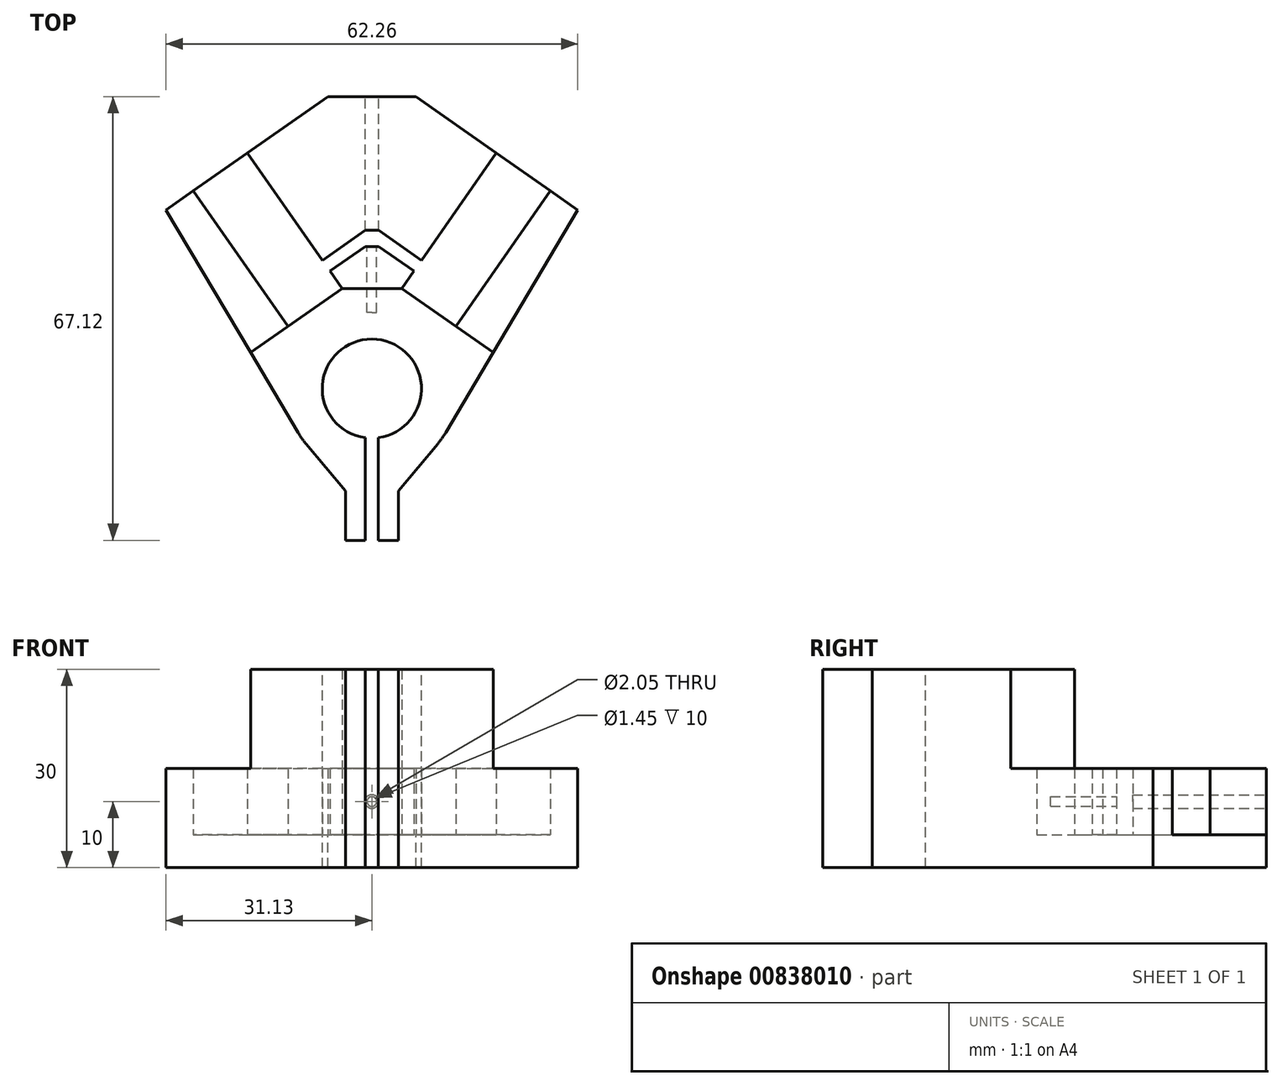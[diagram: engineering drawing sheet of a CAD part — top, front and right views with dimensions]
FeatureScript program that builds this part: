
annotation { "Feature Type Name" : "Feature", "Feature Type Description" : "" }
export const myFeature = defineFeature(function(context is Context, id is Id, definition is map)
    precondition{}
    {
        {
            assignVariable(context, id + "F0", {"name" : "InsertWidth", "anyValue" : 10});
        }
        {
            var Q0;
            Q0=qCreatedBy(makeId("Top.planeOp"),FACE);
            var sketch = newSketch(context, id + "F1", { "sketchPlane" : qUnion([Q0])});
            skPoint(sketch, "E0", {"position": v(-20.9, -11.5) * mm});
            skArc(sketch, "E1", {"start": v(-20.9, -4) * mm, "mid": v(-28.4, -11.5) * mm, "end": v(-20.9, -19) * mm});
            skArc(sketch, "E2", {"start": v(-20.9, 1.5) * mm, "mid": v(-33.9, -11.5) * mm, "end": v(-20.9, -24.5) * mm});
            skLineSegment(sketch, "E3", {"start": v(-20.9, -11.5) * mm, "end": v(-75.55, 66.56) * mm, "construction": true});
            skLineSegment(sketch, "E4", {"start": v(-20.9, -11.5) * mm, "end": v(-20.9, 94.88) * mm, "construction": true});
            skLineSegment(sketch, "E5", {"start": v(-21.62, 32.66) * mm, "end": v(-21.62, 36.51) * mm, "construction": true});
            skLineSegment(sketch, "E6", {"start": v(-33.6, -2.08) * mm, "end": v(-25.4, 3.66) * mm});
            skPoint(sketch, "E7", {"position": v(-29.5, 0.8) * mm});
            skLineSegment(sketch, "E8", {"start": v(-25.4, 3.66) * mm, "end": v(-39.75, 24.14) * mm});
            skPoint(sketch, "E9", {"position": v(-21.62, 0) * mm});
            skLineSegment(sketch, "E10", {"start": v(-21.62, 0) * mm, "end": v(-20.9, 0) * mm});
            skLineSegment(sketch, "E11", {"start": v(-21.62, 0) * mm, "end": v(-21.62, 10) * mm});
            skLineSegment(sketch, "E12", {"start": v(-21.62, 10) * mm, "end": v(-21.92, 10) * mm});
            skLineSegment(sketch, "E13", {"start": v(-21.92, 10) * mm, "end": v(-21.92, 32.66) * mm});
            skLineSegment(sketch, "E14", {"start": v(-33.6, -2.08) * mm, "end": v(-47.94, 18.4) * mm});
            skLineSegment(sketch, "E15", {"start": v(-47.94, 18.4) * mm, "end": v(-39.75, 24.14) * mm});
            skLineSegment(sketch, "E16", {"start": v(-47.94, 18.4) * mm, "end": v(-52.03, 15.53) * mm});
            skLineSegment(sketch, "E17", {"start": v(-39.75, 24.14) * mm, "end": v(-38.93, 24.71) * mm});
            skLineSegment(sketch, "E18", {"start": v(-38.93, 24.71) * mm, "end": v(-21.62, 0) * mm, "construction": true});
            skLineSegment(sketch, "E19", {"start": v(-21.92, 10) * mm, "end": v(-27.24, 6.28) * mm});
            skLineSegment(sketch, "E20", {"start": v(-28.39, 7.92) * mm, "end": v(-21.92, 12.44) * mm});
            skLineSegment(sketch, "E21", {"start": v(-27.57, 8.49) * mm, "end": v(-27.57, 32.66) * mm});
            skLineSegment(sketch, "E22", {"start": v(-38.93, 24.71) * mm, "end": v(-27.57, 32.66) * mm});
            skLineSegment(sketch, "E23", {"start": v(-27.57, 32.66) * mm, "end": v(-20.9, 32.66) * mm});
            skLineSegment(sketch, "E24", {"start": v(-52.03, 15.53) * mm, "end": v(-32.08, -18.12) * mm});
            skPoint(sketch, "E25", {"position": v(-21.9, -24.46) * mm});
            skPoint(sketch, "E26", {"position": v(-21.9, -18.93) * mm});
            skLineSegment(sketch, "E27", {"start": v(-21.9, -18.93) * mm, "end": v(-21.9, -24.46) * mm});
            skLineSegment(sketch, "E28", {"start": v(-21.9, -24.46) * mm, "end": v(-21.9, -34.46) * mm});
            skLineSegment(sketch, "E29", {"start": v(-21.9, -34.46) * mm, "end": v(-24.9, -34.46) * mm});
            skLineSegment(sketch, "E30", {"start": v(-24.9, -34.46) * mm, "end": v(-24.9, -23.87) * mm});
            skPoint(sketch, "E31", {"position": v(-21.9, -29.46) * mm});
            skLineSegment(sketch, "E32", {"start": v(-21.9, -29.46) * mm, "end": v(-24.9, -29.46) * mm, "construction": true});
            skLineSegment(sketch, "E33", {"start": v(-24.9, -29.46) * mm, "end": v(-24.9, -26.96) * mm, "construction": true});
            skLineSegment(sketch, "E34", {"start": v(-24.9, -26.96) * mm, "end": v(-30.86, -19.85) * mm});
            skLineSegment(sketch, "E35.MirrorCS", {"start": v(-20.17, 10) * mm, "end": v(-19.87, 10) * mm});
            skLineSegment(sketch, "E36.MirrorCS", {"start": v(-20.17, 0) * mm, "end": v(-20.9, 0) * mm});
            skLineSegment(sketch, "E37.MirrorCS", {"start": v(-2.05, 24.14) * mm, "end": v(-2.87, 24.71) * mm});
            skLineSegment(sketch, "E38.MirrorCS", {"start": v(-2.87, 24.71) * mm, "end": v(-14.23, 32.66) * mm});
            skLineSegment(sketch, "E39.MirrorCS", {"start": v(-19.9, -18.93) * mm, "end": v(-19.9, -24.46) * mm});
            skLineSegment(sketch, "E40.MirrorCS", {"start": v(6.14, 18.4) * mm, "end": v(10.23, 15.53) * mm});
            skLineSegment(sketch, "E41.MirrorCS", {"start": v(-16.9, -29.46) * mm, "end": v(-16.9, -26.96) * mm, "construction": true});
            skLineSegment(sketch, "E42.MirrorCS", {"start": v(-20.17, 32.66) * mm, "end": v(-20.17, 36.51) * mm, "construction": true});
            skLineSegment(sketch, "E43.MirrorCS", {"start": v(-19.9, -29.46) * mm, "end": v(-16.9, -29.46) * mm, "construction": true});
            skLineSegment(sketch, "E44.MirrorCS", {"start": v(-19.9, -34.46) * mm, "end": v(-16.9, -34.46) * mm});
            skLineSegment(sketch, "E45.MirrorCS", {"start": v(-8.2, -2.08) * mm, "end": v(-16.4, 3.66) * mm});
            skLineSegment(sketch, "E46.MirrorCS", {"start": v(-19.9, -24.46) * mm, "end": v(-19.9, -34.46) * mm});
            skLineSegment(sketch, "E47.MirrorCS", {"start": v(-14.23, 32.66) * mm, "end": v(-20.9, 32.66) * mm});
            skLineSegment(sketch, "E48.MirrorCS", {"start": v(-19.87, 10) * mm, "end": v(-14.56, 6.28) * mm});
            skLineSegment(sketch, "E49.MirrorCS", {"start": v(-19.87, 10) * mm, "end": v(-19.87, 32.66) * mm});
            skLineSegment(sketch, "E50.MirrorCS", {"start": v(-13.41, 7.92) * mm, "end": v(-19.87, 12.44) * mm});
            skLineSegment(sketch, "E51.MirrorCS", {"start": v(-16.9, -26.96) * mm, "end": v(-10.94, -19.85) * mm});
            skLineSegment(sketch, "E52.MirrorCS", {"start": v(10.23, 15.53) * mm, "end": v(-9.72, -18.12) * mm});
            skLineSegment(sketch, "E53.MirrorCS", {"start": v(-8.2, -2.08) * mm, "end": v(6.14, 18.4) * mm});
            skPoint(sketch, "E54.MirrorP", {"position": v(-19.9, -29.46) * mm});
            skLineSegment(sketch, "E55.MirrorCS", {"start": v(-2.87, 24.71) * mm, "end": v(-20.17, 0) * mm, "construction": true});
            skArc(sketch, "E56.MirrorCS", {"start": v(-20.9, 1.5) * mm, "mid": v(-7.9, -11.5) * mm, "end": v(-20.9, -24.5) * mm});
            skPoint(sketch, "E57.MirrorP", {"position": v(-12.3, 0.8) * mm});
            skLineSegment(sketch, "E58.MirrorCS", {"start": v(6.14, 18.4) * mm, "end": v(-2.05, 24.14) * mm});
            skPoint(sketch, "E59.MirrorP", {"position": v(-19.9, -24.46) * mm});
            skLineSegment(sketch, "E60.MirrorCS", {"start": v(-16.9, -34.46) * mm, "end": v(-16.9, -23.87) * mm});
            skLineSegment(sketch, "E61.MirrorCS", {"start": v(-20.17, 0) * mm, "end": v(-20.17, 10) * mm});
            skLineSegment(sketch, "E62.MirrorCS", {"start": v(-16.4, 3.66) * mm, "end": v(-2.05, 24.14) * mm});
            skArc(sketch, "E63.MirrorCS", {"start": v(-20.9, -4) * mm, "mid": v(-13.4, -11.5) * mm, "end": v(-20.9, -19) * mm});
            skLineSegment(sketch, "E64.MirrorCS", {"start": v(-14.23, 8.49) * mm, "end": v(-14.23, 32.66) * mm});
            skPoint(sketch, "E65.MirrorP", {"position": v(-20.17, 0) * mm});
            skPoint(sketch, "E66.MirrorP", {"position": v(-19.9, -18.93) * mm});
            skLineSegment(sketch, "E67", {"start": v(-21.92, 12.44) * mm, "end": v(-19.87, 12.44) * mm});
            skLineSegment(sketch, "E68", {"start": v(-20.17, 10) * mm, "end": v(-21.62, 10) * mm});
            skLineSegment(sketch, "E69", {"start": v(-33.6, -2.08) * mm, "end": v(-39.25, -6.03) * mm});
            skLineSegment(sketch, "E70", {"start": v(-8.2, -2.08) * mm, "end": v(-2.55, -6.03) * mm});
            skLineSegment(sketch, "E71", {"start": v(-25.4, 3.66) * mm, "end": v(-16.4, 3.66) * mm});
            skLineSegment(sketch, "E72", {"start": v(-20.9, -11.5) * mm, "end": v(-37.28, -22.97) * mm, "construction": true});
            skSolve(sketch);
        }
        {
            var Q0;
            {var subQ2=sQuery(id+"F1.wireOp",EDGE,"E21");Q0=makeQuery(id+"F1.imprint","IMPRINT",FACE,{"disambiguationData":[TD([[makeQuery(id+"F1.imprint","IMPRINT",EDGE,{"derivedFrom":subQ2}),1.0]])]});}
            var Q1;
            {var subQ1=sQuery(id+"F1.wireOp",EDGE,"E45.MirrorCS");Q1=makeQuery(id+"F1.imprint","IMPRINT",FACE,{"disambiguationData":[TD([[makeQuery(id+"F1.imprint","IMPRINT",EDGE,{"derivedFrom":subQ1}),-1.0]])]});}
            var Q2;
            {var subQ5=sQuery(id+"F1.wireOp",EDGE,"E27");Q2=makeQuery(id+"F1.imprint","IMPRINT",FACE,{"disambiguationData":[TD([[makeQuery(id+"F1.imprint","IMPRINT",EDGE,{"derivedFrom":subQ5}),-1.0]])]});}
            var Q3;
            {var subQ1=sQuery(id+"F1.wireOp",EDGE,"E12");Q3=makeQuery(id+"F1.imprint","IMPRINT",FACE,{"disambiguationData":[TD([[makeQuery(id+"F1.imprint","IMPRINT",EDGE,{"derivedFrom":subQ1}),1.0]])]});}
            var Q4;
            {var subQ4=sQuery(id+"F1.wireOp",EDGE,"E44.MirrorCS");Q4=makeQuery(id+"F1.imprint","IMPRINT",FACE,{"disambiguationData":[TD([[makeQuery(id+"F1.imprint","IMPRINT",EDGE,{"derivedFrom":subQ4}),1.0]])]});}
            var Q5;
            Q5=makeQuery(id+"F1.imprint","IMPRINT",FACE,{"disambiguationData":[TD([[makeQuery(id+"F1.imprint","IMPRINT",EDGE,{"derivedFrom":sQuery(id+"F1.wireOp",EDGE,"E14")}),1.0]])]});
            var Q6;
            {var subQ0=sQuery(id+"F1.wireOp",EDGE,"E40.MirrorCS");Q6=makeQuery(id+"F1.imprint","IMPRINT",FACE,{"disambiguationData":[TD([[makeQuery(id+"F1.imprint","IMPRINT",EDGE,{"derivedFrom":subQ0}),-1.0]])]});}
            var Q7;
            {var subQ3=sQuery(id+"F1.wireOp",EDGE,"E19");var subQ5=sQuery(id+"F1.wireOp",EDGE,"E18");var subQ6=makeQuery(id+"F1.imprint","INTERSECT",VERTEX,{"derivedFrom":[subQ5,subQ3]});Q7=makeQuery(id+"F1.imprint","IMPRINT",FACE,{"disambiguationData":[TD([[makeQuery(id+"F1.imprint","IMPRINT",EDGE,{"disambiguationData":[TD([[subQ6,-1.0]])],"derivedFrom":subQ5}),-1.0]])]});}
            var Q8;
            {var subQ1=sQuery(id+"F1.wireOp",EDGE,"E35.MirrorCS");Q8=makeQuery(id+"F1.imprint","IMPRINT",FACE,{"disambiguationData":[TD([[makeQuery(id+"F1.imprint","IMPRINT",EDGE,{"derivedFrom":subQ1}),-1.0]])]});}
            var Q9;
            {var subQ0=sQuery(id+"F1.wireOp",EDGE,"E19");var subQ5=sQuery(id+"F1.wireOp",EDGE,"E18");var subQ6=makeQuery(id+"F1.imprint","INTERSECT",VERTEX,{"derivedFrom":[subQ5,subQ0]});Q9=makeQuery(id+"F1.imprint","IMPRINT",FACE,{"disambiguationData":[TD([[makeQuery(id+"F1.imprint","IMPRINT",EDGE,{"disambiguationData":[TD([[subQ6,1.0]])],"derivedFrom":subQ5}),1.0]])]});}
            var Q10;
            {var subQ3=sQuery(id+"F1.wireOp",EDGE,"E28");Q10=makeQuery(id+"F1.imprint","IMPRINT",FACE,{"disambiguationData":[TD([[makeQuery(id+"F1.imprint","IMPRINT",EDGE,{"derivedFrom":subQ3}),-1.0]])]});}
            var Q11;
            {var subQ0=sQuery(id+"F1.wireOp",EDGE,"E51.MirrorCS");Q11=makeQuery(id+"F1.imprint","IMPRINT",FACE,{"disambiguationData":[TD([[makeQuery(id+"F1.imprint","IMPRINT",EDGE,{"derivedFrom":subQ0}),1.0]])]});}
            var Q12;
            {var subQ4=sQuery(id+"F1.wireOp",EDGE,"E6");Q12=makeQuery(id+"F1.imprint","IMPRINT",FACE,{"disambiguationData":[TD([[makeQuery(id+"F1.imprint","IMPRINT",EDGE,{"derivedFrom":subQ4}),1.0]])]});}
            var Q13;
            {var subQ0=sQuery(id+"F1.wireOp",EDGE,"E38.MirrorCS");Q13=makeQuery(id+"F1.imprint","IMPRINT",FACE,{"disambiguationData":[TD([[makeQuery(id+"F1.imprint","IMPRINT",EDGE,{"derivedFrom":subQ0}),1.0]])]});}
            var Q14;
            {var subQ0=sQuery(id+"F1.wireOp",EDGE,"E37.MirrorCS");Q14=makeQuery(id+"F1.imprint","IMPRINT",FACE,{"disambiguationData":[TD([[makeQuery(id+"F1.imprint","IMPRINT",EDGE,{"derivedFrom":subQ0}),1.0]])]});}
            var Q15;
            {var subQ0=sQuery(id+"F1.wireOp",EDGE,"E68");Q15=makeQuery(id+"F1.imprint","IMPRINT",FACE,{"disambiguationData":[TD([[makeQuery(id+"F1.imprint","IMPRINT",EDGE,{"derivedFrom":subQ0}),1.0]])]});}
            var Q16;
            {var subQ3=sQuery(id+"F1.wireOp",EDGE,"E34");Q16=makeQuery(id+"F1.imprint","IMPRINT",FACE,{"disambiguationData":[TD([[makeQuery(id+"F1.imprint","IMPRINT",EDGE,{"derivedFrom":subQ3}),-1.0]])]});}
            var Q17;
            {var subQ5=sQuery(id+"F1.wireOp",EDGE,"E21");Q17=makeQuery(id+"F1.imprint","IMPRINT",FACE,{"disambiguationData":[TD([[makeQuery(id+"F1.imprint","IMPRINT",EDGE,{"derivedFrom":subQ5}),-1.0]])]});}
            var Q18;
            {var subQ3=sQuery(id+"F1.wireOp",EDGE,"E67");Q18=makeQuery(id+"F1.imprint","IMPRINT",FACE,{"disambiguationData":[TD([[makeQuery(id+"F1.imprint","IMPRINT",EDGE,{"derivedFrom":subQ3}),1.0]])]});}
            var Q19;
            {var subQ15=sQuery(id+"F1.wireOp",EDGE,"E6");Q19=makeQuery(id+"F1.imprint","IMPRINT",FACE,{"disambiguationData":[TD([[makeQuery(id+"F1.imprint","IMPRINT",EDGE,{"derivedFrom":subQ15}),-1.0]])]});}
            var Q20;
            {var subQ0=sQuery(id+"F1.wireOp",EDGE,"E64.MirrorCS");Q20=makeQuery(id+"F1.imprint","IMPRINT",FACE,{"disambiguationData":[TD([[makeQuery(id+"F1.imprint","IMPRINT",EDGE,{"derivedFrom":subQ0}),1.0]])]});}
            var Q21;
            {var subQ0=sQuery(id+"F1.wireOp",EDGE,"E17");Q21=makeQuery(id+"F1.imprint","IMPRINT",FACE,{"disambiguationData":[TD([[makeQuery(id+"F1.imprint","IMPRINT",EDGE,{"derivedFrom":subQ0}),-1.0]])]});}
            var Q22;
            {var subQ1=sQuery(id+"F1.wireOp",EDGE,"E48.MirrorCS");var subQ3=sQuery(id+"F1.wireOp",EDGE,"E55.MirrorCS");var subQ4=makeQuery(id+"F1.imprint","INTERSECT",VERTEX,{"derivedFrom":[subQ1,subQ3]});Q22=makeQuery(id+"F1.imprint","IMPRINT",FACE,{"disambiguationData":[TD([[makeQuery(id+"F1.imprint","IMPRINT",EDGE,{"disambiguationData":[TD([[subQ4,1.0]])],"derivedFrom":subQ1}),1.0]])]});}
            var Q23;
            {var subQ0=sQuery(id+"F1.wireOp",EDGE,"E62.MirrorCS");var subQ1=sQuery(id+"F1.wireOp",EDGE,"E48.MirrorCS");var subQ2=makeQuery(id+"F1.imprint","INTERSECT",VERTEX,{"derivedFrom":[subQ1,subQ0]});Q23=makeQuery(id+"F1.imprint","IMPRINT",FACE,{"disambiguationData":[TD([[makeQuery(id+"F1.imprint","IMPRINT",EDGE,{"disambiguationData":[TD([[subQ2,1.0]])],"derivedFrom":subQ1}),-1.0]])]});}
            var Q24;
            {var subQ1=sQuery(id+"F1.wireOp",EDGE,"E11");var subQ3=sQuery(id+"F1.wireOp",EDGE,"E71");var subQ4=makeQuery(id+"F1.imprint","INTERSECT",VERTEX,{"derivedFrom":[subQ1,subQ3]});Q24=makeQuery(id+"F1.imprint","IMPRINT",FACE,{"disambiguationData":[TD([[makeQuery(id+"F1.imprint","IMPRINT",EDGE,{"disambiguationData":[TD([[subQ4,1.0]])],"derivedFrom":subQ3}),-1.0]])]});}
            var Q25;
            {var subQ1=sQuery(id+"F1.wireOp",EDGE,"E55.MirrorCS");var subQ3=sQuery(id+"F1.wireOp",EDGE,"E71");var subQ4=makeQuery(id+"F1.imprint","INTERSECT",VERTEX,{"derivedFrom":[subQ1,subQ3]});Q25=makeQuery(id+"F1.imprint","IMPRINT",FACE,{"disambiguationData":[TD([[makeQuery(id+"F1.imprint","IMPRINT",EDGE,{"disambiguationData":[TD([[subQ4,1.0]])],"derivedFrom":subQ3}),-1.0]])]});}
            var Q26;
            {var subQ5=sQuery(id+"F1.wireOp",EDGE,"E10");Q26=makeQuery(id+"F1.imprint","IMPRINT",FACE,{"disambiguationData":[TD([[makeQuery(id+"F1.imprint","IMPRINT",EDGE,{"derivedFrom":subQ5}),1.0]])]});}
            var Q27;
            {var subQ0=sQuery(id+"F1.wireOp",EDGE,"E62.MirrorCS");var subQ1=sQuery(id+"F1.wireOp",EDGE,"E48.MirrorCS");var subQ2=makeQuery(id+"F1.imprint","INTERSECT",VERTEX,{"derivedFrom":[subQ1,subQ0]});Q27=makeQuery(id+"F1.imprint","IMPRINT",FACE,{"disambiguationData":[TD([[makeQuery(id+"F1.imprint","IMPRINT",EDGE,{"disambiguationData":[TD([[subQ2,1.0]])],"derivedFrom":subQ1}),1.0]])]});}
            var Q28;
            {var subQ0=sQuery(id+"F1.wireOp",EDGE,"E19");var subQ1=sQuery(id+"F1.wireOp",EDGE,"E8");var subQ2=makeQuery(id+"F1.imprint","INTERSECT",VERTEX,{"derivedFrom":[subQ1,subQ0]});Q28=makeQuery(id+"F1.imprint","IMPRINT",FACE,{"disambiguationData":[TD([[makeQuery(id+"F1.imprint","IMPRINT",EDGE,{"disambiguationData":[TD([[subQ2,-1.0]])],"derivedFrom":subQ1}),-1.0]])]});}
            var Q29;
            {var subQ2=sQuery(id+"F1.wireOp",EDGE,"E12");Q29=makeQuery(id+"F1.imprint","IMPRINT",FACE,{"disambiguationData":[TD([[makeQuery(id+"F1.imprint","IMPRINT",EDGE,{"derivedFrom":subQ2}),-1.0]])]});}
            var Q30;
            {var subQ8=sQuery(id+"F1.wireOp",EDGE,"E45.MirrorCS");Q30=makeQuery(id+"F1.imprint","IMPRINT",FACE,{"disambiguationData":[TD([[makeQuery(id+"F1.imprint","IMPRINT",EDGE,{"derivedFrom":subQ8}),1.0]])]});}
            extrude(context, id + "F2", {"entities" : qUnion([Q0, Q1, Q2, Q3, Q4, Q5, Q6, Q7, Q8, Q9, Q10, Q11, Q12, Q13, Q14, Q15, Q16, Q17, Q18, Q19, Q20, Q21, Q22, Q23, Q24, Q25, Q26, Q27, Q28, Q29, Q30]), "oppositeDirection" : true, "depth" : 5 * mm, "offsetDistance" : 25 * mm});
        }
        {
            var Q0;
            {var subQ0=sQuery(id+"F1.wireOp",EDGE,"E64.MirrorCS");Q0=makeQuery(id+"F1.imprint","IMPRINT",FACE,{"disambiguationData":[TD([[makeQuery(id+"F1.imprint","IMPRINT",EDGE,{"derivedFrom":subQ0}),1.0]])]});}
            var Q1;
            {var subQ5=sQuery(id+"F1.wireOp",EDGE,"E21");Q1=makeQuery(id+"F1.imprint","IMPRINT",FACE,{"disambiguationData":[TD([[makeQuery(id+"F1.imprint","IMPRINT",EDGE,{"derivedFrom":subQ5}),-1.0]])]});}
            var Q2;
            {var subQ2=sQuery(id+"F1.wireOp",EDGE,"E21");Q2=makeQuery(id+"F1.imprint","IMPRINT",FACE,{"disambiguationData":[TD([[makeQuery(id+"F1.imprint","IMPRINT",EDGE,{"derivedFrom":subQ2}),1.0]])]});}
            var Q3;
            {var subQ0=sQuery(id+"F1.wireOp",EDGE,"E17");Q3=makeQuery(id+"F1.imprint","IMPRINT",FACE,{"disambiguationData":[TD([[makeQuery(id+"F1.imprint","IMPRINT",EDGE,{"derivedFrom":subQ0}),-1.0]])]});}
            var Q4;
            {var subQ0=sQuery(id+"F1.wireOp",EDGE,"E38.MirrorCS");Q4=makeQuery(id+"F1.imprint","IMPRINT",FACE,{"disambiguationData":[TD([[makeQuery(id+"F1.imprint","IMPRINT",EDGE,{"derivedFrom":subQ0}),1.0]])]});}
            var Q5;
            {var subQ0=sQuery(id+"F1.wireOp",EDGE,"E37.MirrorCS");Q5=makeQuery(id+"F1.imprint","IMPRINT",FACE,{"disambiguationData":[TD([[makeQuery(id+"F1.imprint","IMPRINT",EDGE,{"derivedFrom":subQ0}),1.0]])]});}
            var Q6;
            {var subQ3=sQuery(id+"F1.wireOp",EDGE,"E67");Q6=makeQuery(id+"F1.imprint","IMPRINT",FACE,{"disambiguationData":[TD([[makeQuery(id+"F1.imprint","IMPRINT",EDGE,{"derivedFrom":subQ3}),1.0]])]});}
            extrude(context, id + "F3", {"entities" : qUnion([Q0, Q1, Q2, Q3, Q4, Q5, Q6]), "depth" : (getVariable(context, 'InsertWidth')) * mm, "offsetDistance" : 25 * mm});
        }
        {
            var Q0;
            Q0=makeQuery(id+"F3.opExtrude","SWEPT_FACE",FACE,{"disambiguationData":[OSD([sQuery(id+"F1.wireOp",EDGE,"E23"),sQuery(id+"F1.wireOp",EDGE,"E47.MirrorCS")])]});
            var sketch = newSketch(context, id + "F4", { "sketchPlane" : qUnion([Q0])});
            skPoint(sketch, "E73.0", {"position": v(20.9, 0) * mm});
            skPoint(sketch, "E73.1", {"position": v(21.62, 0) * mm});
            skPoint(sketch, "E73.2", {"position": v(21.92, 0) * mm});
            skPoint(sketch, "E73.3", {"position": v(20.17, 0) * mm});
            skPoint(sketch, "E73.4", {"position": v(19.87, 0) * mm});
            skLineSegment(sketch, "E74", {"start": v(20.9, 0) * mm, "end": v(20.9, 10) * mm, "construction": true});
            skPoint(sketch, "E75", {"position": v(20.9, 5) * mm});
            skLineSegment(sketch, "E76", {"start": v(21.62, 0) * mm, "end": v(21.62, 10) * mm, "construction": true});
            skLineSegment(sketch, "E77", {"start": v(21.92, 0) * mm, "end": v(21.92, 10) * mm, "construction": true});
            skCircle(sketch, "E78", {"center": v(20.9, 5) * mm, "radius": 0.73 * mm});
            skCircle(sketch, "E79", {"center": v(20.9, 5) * mm, "radius": 1.03 * mm});
            skSolve(sketch);
        }
        {
            var Q0;
            {var subQ15=sQuery(id+"F1.wireOp",EDGE,"E6");Q0=makeQuery(id+"F1.imprint","IMPRINT",FACE,{"disambiguationData":[TD([[makeQuery(id+"F1.imprint","IMPRINT",EDGE,{"derivedFrom":subQ15}),-1.0]])]});}
            var Q1;
            {var subQ5=sQuery(id+"F1.wireOp",EDGE,"E27");Q1=makeQuery(id+"F1.imprint","IMPRINT",FACE,{"disambiguationData":[TD([[makeQuery(id+"F1.imprint","IMPRINT",EDGE,{"derivedFrom":subQ5}),-1.0]])]});}
            var Q2;
            {var subQ3=sQuery(id+"F1.wireOp",EDGE,"E28");Q2=makeQuery(id+"F1.imprint","IMPRINT",FACE,{"disambiguationData":[TD([[makeQuery(id+"F1.imprint","IMPRINT",EDGE,{"derivedFrom":subQ3}),-1.0]])]});}
            var Q3;
            {var subQ3=sQuery(id+"F1.wireOp",EDGE,"E34");Q3=makeQuery(id+"F1.imprint","IMPRINT",FACE,{"disambiguationData":[TD([[makeQuery(id+"F1.imprint","IMPRINT",EDGE,{"derivedFrom":subQ3}),-1.0]])]});}
            var Q4;
            {var subQ0=sQuery(id+"F1.wireOp",EDGE,"E51.MirrorCS");Q4=makeQuery(id+"F1.imprint","IMPRINT",FACE,{"disambiguationData":[TD([[makeQuery(id+"F1.imprint","IMPRINT",EDGE,{"derivedFrom":subQ0}),1.0]])]});}
            var Q5;
            {var subQ4=sQuery(id+"F1.wireOp",EDGE,"E44.MirrorCS");Q5=makeQuery(id+"F1.imprint","IMPRINT",FACE,{"disambiguationData":[TD([[makeQuery(id+"F1.imprint","IMPRINT",EDGE,{"derivedFrom":subQ4}),1.0]])]});}
            var Q6;
            {var subQ1=sQuery(id+"F1.wireOp",EDGE,"E55.MirrorCS");var subQ3=sQuery(id+"F1.wireOp",EDGE,"E71");var subQ4=makeQuery(id+"F1.imprint","INTERSECT",VERTEX,{"derivedFrom":[subQ1,subQ3]});Q6=makeQuery(id+"F1.imprint","IMPRINT",FACE,{"disambiguationData":[TD([[makeQuery(id+"F1.imprint","IMPRINT",EDGE,{"disambiguationData":[TD([[subQ4,1.0]])],"derivedFrom":subQ3}),-1.0]])]});}
            var Q7;
            {var subQ1=sQuery(id+"F1.wireOp",EDGE,"E11");var subQ3=sQuery(id+"F1.wireOp",EDGE,"E71");var subQ4=makeQuery(id+"F1.imprint","INTERSECT",VERTEX,{"derivedFrom":[subQ1,subQ3]});Q7=makeQuery(id+"F1.imprint","IMPRINT",FACE,{"disambiguationData":[TD([[makeQuery(id+"F1.imprint","IMPRINT",EDGE,{"disambiguationData":[TD([[subQ4,1.0]])],"derivedFrom":subQ3}),-1.0]])]});}
            var Q8;
            {var subQ5=sQuery(id+"F1.wireOp",EDGE,"E10");Q8=makeQuery(id+"F1.imprint","IMPRINT",FACE,{"disambiguationData":[TD([[makeQuery(id+"F1.imprint","IMPRINT",EDGE,{"derivedFrom":subQ5}),1.0]])]});}
            var Q9;
            {var subQ8=sQuery(id+"F1.wireOp",EDGE,"E45.MirrorCS");Q9=makeQuery(id+"F1.imprint","IMPRINT",FACE,{"disambiguationData":[TD([[makeQuery(id+"F1.imprint","IMPRINT",EDGE,{"derivedFrom":subQ8}),1.0]])]});}
            extrude(context, id + "F5", {"entities" : qUnion([Q0, Q1, Q2, Q3, Q4, Q5, Q6, Q7, Q8, Q9]), "operationType" : NewBodyOperationType.ADD, "depth" : 25 * mm, "offsetDistance" : 25 * mm});
        }
        {
            var Q0;
            {var subQ7=sQuery(id+"F1.wireOp",EDGE,"E27");Q0=makeQuery(id+"F1.imprint","IMPRINT",FACE,{"disambiguationData":[TD([[makeQuery(id+"F1.imprint","IMPRINT",EDGE,{"derivedFrom":subQ7}),-1.0]])]});}
            var Q1;
            {var subQ3=sQuery(id+"F1.wireOp",EDGE,"E34");Q1=makeQuery(id+"F1.imprint","IMPRINT",FACE,{"disambiguationData":[TD([[makeQuery(id+"F1.imprint","IMPRINT",EDGE,{"derivedFrom":subQ3}),-1.0]])]});}
            var Q2;
            {var subQ1=sQuery(id+"F1.wireOp",EDGE,"E28");Q2=makeQuery(id+"F1.imprint","IMPRINT",FACE,{"disambiguationData":[TD([[makeQuery(id+"F1.imprint","IMPRINT",EDGE,{"derivedFrom":subQ1}),-1.0]])]});}
            var Q3;
            {var subQ1=sQuery(id+"F1.wireOp",EDGE,"E44.MirrorCS");Q3=makeQuery(id+"F1.imprint","IMPRINT",FACE,{"disambiguationData":[TD([[makeQuery(id+"F1.imprint","IMPRINT",EDGE,{"derivedFrom":subQ1}),1.0]])]});}
            var Q4;
            {var subQ0=sQuery(id+"F1.wireOp",EDGE,"E51.MirrorCS");Q4=makeQuery(id+"F1.imprint","IMPRINT",FACE,{"disambiguationData":[TD([[makeQuery(id+"F1.imprint","IMPRINT",EDGE,{"derivedFrom":subQ0}),1.0]])]});}
            var Q5;
            {var subQ3=sQuery(id+"F1.wireOp",EDGE,"wE3qk1zT-ZEZv-AR1l-YeVC-WgNcCrWfGm45");Q5=makeQuery(id+"F1.imprint","IMPRINT",FACE,{"disambiguationData":[TD([[makeQuery(id+"F1.imprint","IMPRINT",EDGE,{"derivedFrom":subQ3}),-1.0]])]});}
            var Q6;
            {var subQ3=sQuery(id+"F1.wireOp",EDGE,"uzH9pRL8-awsT-I6LR-pqOu-2XfLFLQ0b1Ti");Q6=makeQuery(id+"F1.imprint","IMPRINT",FACE,{"disambiguationData":[TD([[makeQuery(id+"F1.imprint","IMPRINT",EDGE,{"derivedFrom":subQ3}),1.0]])]});}
            var Q7;
            Q7=makeQuery(id+"F1.imprint","IMPRINT",FACE,{"disambiguationData":[TD([[makeQuery(id+"F1.imprint","IMPRINT",EDGE,{"derivedFrom":sQuery(id+"F1.wireOp",EDGE,"E14")}),1.0]])]});
            var Q8;
            {var subQ0=sQuery(id+"F1.wireOp",EDGE,"E40.MirrorCS");Q8=makeQuery(id+"F1.imprint","IMPRINT",FACE,{"disambiguationData":[TD([[makeQuery(id+"F1.imprint","IMPRINT",EDGE,{"derivedFrom":subQ0}),-1.0]])]});}
            var Q9;
            {var subQ15=sQuery(id+"F1.wireOp",EDGE,"E6");Q9=makeQuery(id+"F1.imprint","IMPRINT",FACE,{"disambiguationData":[TD([[makeQuery(id+"F1.imprint","IMPRINT",EDGE,{"derivedFrom":subQ15}),-1.0]])]});}
            var Q10;
            {var subQ1=sQuery(id+"F1.wireOp",EDGE,"E55.MirrorCS");var subQ3=sQuery(id+"F1.wireOp",EDGE,"E71");var subQ4=makeQuery(id+"F1.imprint","INTERSECT",VERTEX,{"derivedFrom":[subQ1,subQ3]});Q10=makeQuery(id+"F1.imprint","IMPRINT",FACE,{"disambiguationData":[TD([[makeQuery(id+"F1.imprint","IMPRINT",EDGE,{"disambiguationData":[TD([[subQ4,1.0]])],"derivedFrom":subQ3}),-1.0]])]});}
            var Q11;
            {var subQ5=sQuery(id+"F1.wireOp",EDGE,"E10");Q11=makeQuery(id+"F1.imprint","IMPRINT",FACE,{"disambiguationData":[TD([[makeQuery(id+"F1.imprint","IMPRINT",EDGE,{"derivedFrom":subQ5}),1.0]])]});}
            var Q12;
            {var subQ1=sQuery(id+"F1.wireOp",EDGE,"E11");var subQ3=sQuery(id+"F1.wireOp",EDGE,"E71");var subQ4=makeQuery(id+"F1.imprint","INTERSECT",VERTEX,{"derivedFrom":[subQ1,subQ3]});Q12=makeQuery(id+"F1.imprint","IMPRINT",FACE,{"disambiguationData":[TD([[makeQuery(id+"F1.imprint","IMPRINT",EDGE,{"disambiguationData":[TD([[subQ4,1.0]])],"derivedFrom":subQ3}),-1.0]])]});}
            var Q13;
            {var subQ8=sQuery(id+"F1.wireOp",EDGE,"E45.MirrorCS");Q13=makeQuery(id+"F1.imprint","IMPRINT",FACE,{"disambiguationData":[TD([[makeQuery(id+"F1.imprint","IMPRINT",EDGE,{"derivedFrom":subQ8}),1.0]])]});}
            var Q14;
            {var subQ5=sQuery(id+"F1.wireOp",EDGE,"E35.MirrorCS");Q14=makeQuery(id+"F1.imprint","IMPRINT",FACE,{"disambiguationData":[TD([[makeQuery(id+"F1.imprint","IMPRINT",EDGE,{"derivedFrom":subQ5}),-1.0]])]});}
            var Q15;
            {var subQ1=sQuery(id+"F1.wireOp",EDGE,"E12");Q15=makeQuery(id+"F1.imprint","IMPRINT",FACE,{"disambiguationData":[TD([[makeQuery(id+"F1.imprint","IMPRINT",EDGE,{"derivedFrom":subQ1}),1.0]])]});}
            var Q16;
            {var subQ0=sQuery(id+"F1.wireOp",EDGE,"E68");Q16=makeQuery(id+"F1.imprint","IMPRINT",FACE,{"disambiguationData":[TD([[makeQuery(id+"F1.imprint","IMPRINT",EDGE,{"derivedFrom":subQ0}),1.0]])]});}
            extrude(context, id + "F6", {"entities" : qUnion([Q0, Q1, Q2, Q3, Q4, Q5, Q6, Q7, Q8, Q9, Q10, Q11, Q12, Q13, Q14, Q15, Q16]), "operationType" : NewBodyOperationType.ADD, "depth" : (getVariable(context, 'InsertWidth')) * mm, "offsetDistance" : 25 * mm});
        }
        {
            var Q0;
            Q0=makeQuery(id+"F4.imprint","IMPRINT",FACE,{"disambiguationData":[TD([[makeQuery(id+"F4.imprint","IMPRINT",EDGE,{"derivedFrom":sQuery(id+"F4.wireOp",EDGE,"E78")}),1.0]])]});
            var Q1;
            Q1=qCreatedBy(makeId("Front.planeOp"),FACE);
            extrude(context, id + "F7", {"entities" : qUnion([Q0]), "operationType" : NewBodyOperationType.REMOVE, "endBound" : BoundingType.UP_TO_SURFACE, "oppositeDirection" : true, "depth" : 25 * mm, "endBoundEntityFace" : qUnion([Q1]), "offsetDistance" : 25 * mm});
        }
        {
            var Q0;
            Q0=makeQuery(id+"F4.imprint","IMPRINT",FACE,{"disambiguationData":[TD([[makeQuery(id+"F4.imprint","IMPRINT",EDGE,{"derivedFrom":sQuery(id+"F4.wireOp",EDGE,"E78")}),-1.0]])]});
            var Q1;
            Q1=makeQuery(id+"F3.opExtrude","SWEPT_FACE",FACE,{"disambiguationData":[OSD([sQuery(id+"F1.wireOp",EDGE,"E67")])]});
            extrude(context, id + "F8", {"entities" : qUnion([Q0]), "operationType" : NewBodyOperationType.REMOVE, "endBound" : BoundingType.UP_TO_SURFACE, "oppositeDirection" : true, "depth" : 25 * mm, "endBoundEntityFace" : qUnion([Q1]), "offsetDistance" : 25 * mm});
        }
    });
